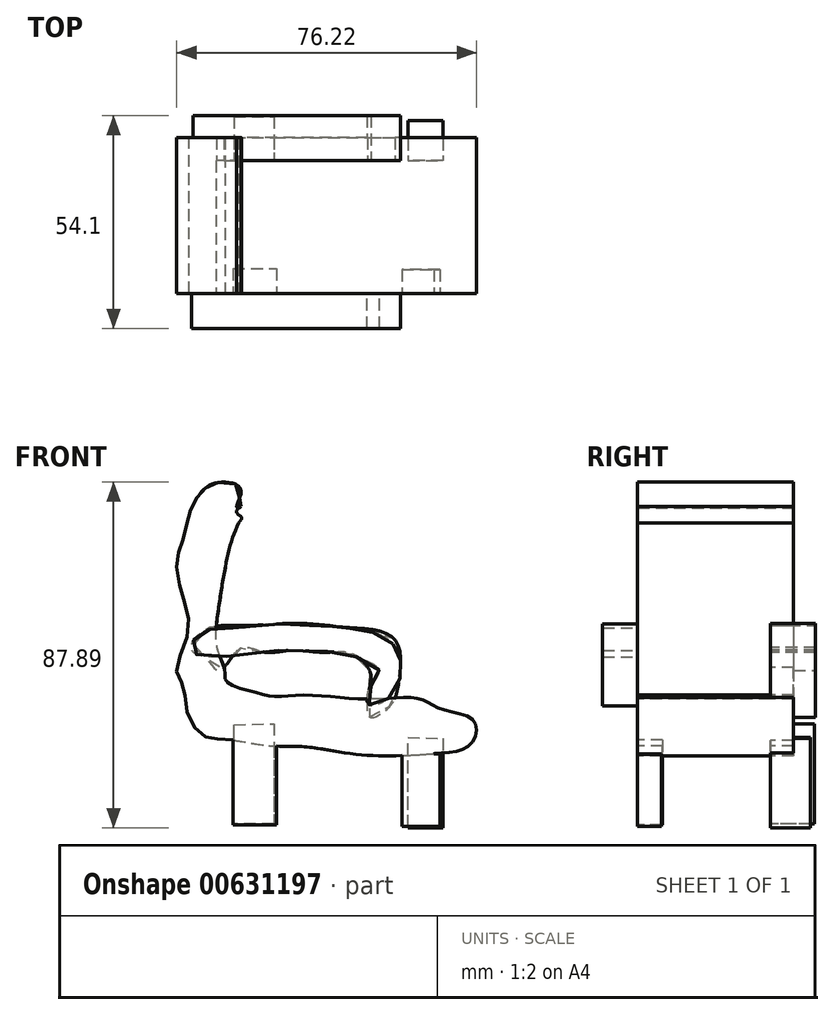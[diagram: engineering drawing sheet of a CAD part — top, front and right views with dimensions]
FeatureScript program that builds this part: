
annotation { "Feature Type Name" : "Feature", "Feature Type Description" : "" }
export const myFeature = defineFeature(function(context is Context, id is Id, definition is map)
    precondition{}
    {
        {
            var Q0;
            Q0=qCreatedBy(makeId("Front.planeOp"),FACE);
            var sketch = newSketch(context, id + "F0", { "sketchPlane" : qUnion([Q0])});
            skFitSpline(sketch, "E0", {"points": [v(-32.6, 41.62) * mm, v(-32.63, 45.08) * mm, v(-38.39, 47.76) * mm, v(-42.92, 45.16) * mm, v(-45.8, 40) * mm, v(-47.39, 33.25) * mm, v(-48.99, 27.76) * mm, v(-47.37, 18.5) * mm, v(-46.09, 9.77) * mm, v(-49, 0) * mm, v(-47.36, -4.04) * mm, v(-46.13, -11.42) * mm, v(-41.64, -16.92) * mm, v(-36.74, -17.5) * mm, v(-25.54, -19.12) * mm, v(-16.21, -19.42) * mm, v(-5.62, -21.05) * mm, v(6.26, -21.69) * mm, v(17.82, -21.06) * mm, v(25.6, -18.86) * mm, v(26.58, -12.94) * mm, v(18.16, -9.8) * mm, v(12.68, -7.2) * mm, v(3.37, -7.23) * mm, v(-7.23, -6.9) * mm, v(-17.8, -6.25) * mm, v(-24.25, -6.6) * mm, v(-30.04, -5.31) * mm, v(-36.45, -2.76) * mm, v(-36.78, 0) * mm, v(-38.68, 5.64) * mm, v(-38.4, 15.58) * mm, v(-36.78, 25.52) * mm, v(-35.04, 32.96) * mm, v(-32.57, 38.94) * mm], "startDerivative": vector(-388.44, -209.27) * mm, "endDerivative": vector(110.78, 242.37) * mm});
            skFitSpline(sketch, "E1", {"points": [v(-32.6, 41.62) * mm, v(-32.57, 38.94) * mm, v(-33.58, 36.74) * mm], "startDerivative": vector(-15.11, -8.14) * mm, "endDerivative": vector(-1.6, -6.6) * mm});
            skSolve(sketch);
        }
        {
            var Q0;
            Q0 = qSketchRegion(id + "F0", true);
            extrude(context, id + "F1", {"entities" : qUnion([Q0]), "oppositeDirection" : true, "depth" : 39.62 * mm, "offsetDistance" : 25.4 * mm});
        }
        {
            var Q0;
            Q0=qCreatedBy(makeId("Front.planeOp"),FACE);
            var sketch = newSketch(context, id + "F2", { "sketchPlane" : qUnion([Q0])});
            skFitSpline(sketch, "E2", {"points": [v(-40.63, 10.44) * mm, v(-32.92, 10.76) * mm, v(-25.54, 11.72) * mm, v(-14.61, 11.4) * mm, v(-8.2, 11.08) * mm, v(-3.37, 10.44) * mm, v(4.34, 8.2) * mm, v(7.55, 3.7) * mm, v(7.87, 0) * mm, v(5.94, -5.94) * mm, v(0, -8.83) * mm, v(0, -4.66) * mm, v(2.4, 0) * mm, v(-6.9, 4.34) * mm, v(-15.9, 4.98) * mm, v(-24.25, 4.98) * mm, v(-31.96, 4.01) * mm, v(-44.49, 4.34) * mm, v(-44.8, 7.55) * mm, v(-40.63, 10.44) * mm]});
            skSolve(sketch);
        }
        {
            var Q0;
            Q0=makeQuery(id+"F2.imprint","IMPRINT",FACE,{"disambiguationData":[TD([[makeQuery(id+"F2.imprint","IMPRINT",EDGE,{"derivedFrom":sQuery(id+"F2.wireOp",EDGE,"E2")}),-1.0]])]});
            extrude(context, id + "F3", {"entities" : qUnion([Q0]), "operationType" : NewBodyOperationType.ADD, "depth" : 8.9 * mm, "offsetDistance" : 25.4 * mm});
        }
        {
            var Q0;
            Q0=qCreatedBy(makeId("Front.planeOp"),FACE);
            var sketch = newSketch(context, id + "F4", { "sketchPlane" : qUnion([Q0])});
            skLineSegment(sketch, "E3", {"start": v(17.83, -21.36) * mm, "end": v(17.83, -39.67) * mm});
            skLineSegment(sketch, "E4", {"start": v(17.83, -39.67) * mm, "end": v(8.2, -39.67) * mm});
            skLineSegment(sketch, "E5", {"start": v(8.2, -39.67) * mm, "end": v(8.2, -23.29) * mm});
            skLineSegment(sketch, "E6", {"start": v(8.2, -23.29) * mm, "end": v(8.2, -20.07) * mm});
            skLineSegment(sketch, "E7", {"start": v(8.2, -20.07) * mm, "end": v(17.83, -21.36) * mm});
            skSolve(sketch);
        }
        {
            var Q0;
            Q0 = qSketchRegion(id + "F4", true);
            extrude(context, id + "F5", {"entities" : qUnion([Q0]), "operationType" : NewBodyOperationType.ADD, "oppositeDirection" : true, "depth" : 6.1 * mm, "offsetDistance" : 25.4 * mm});
        }
        {
            var Q0;
            Q0=qCreatedBy(makeId("Front.planeOp"),FACE);
            var sketch = newSketch(context, id + "F6", { "sketchPlane" : qUnion([Q0])});
            skLineSegment(sketch, "E8", {"start": v(-34.72, -14.2) * mm, "end": v(-34.72, -39.3) * mm});
            skLineSegment(sketch, "E9", {"start": v(-34.72, -39.3) * mm, "end": v(-23.6, -39.3) * mm});
            skLineSegment(sketch, "E10", {"start": v(-23.6, -39.3) * mm, "end": v(-23.6, -14.08) * mm});
            skLineSegment(sketch, "E11", {"start": v(-23.6, -14.08) * mm, "end": v(-34.72, -14.2) * mm});
            skSolve(sketch);
        }
        {
            var Q0;
            Q0 = qSketchRegion(id + "F6", true);
            extrude(context, id + "F7", {"entities" : qUnion([Q0]), "operationType" : NewBodyOperationType.ADD, "oppositeDirection" : true, "depth" : 6.35 * mm, "offsetDistance" : 25.4 * mm});
        }
        {
            var Q0;
            Q0=qCreatedBy(makeId("Front.planeOp"),FACE);
            cPlane(context, id + "F8", {"entities" : qUnion([Q0]), "cplaneType" : CPlaneType.OFFSET, "offset" : 33.78 * mm, "oppositeDirection" : true, "width" : 152.4 * mm, "height" : 152.4 * mm});
        }
        {
            var Q0;
            Q0=qCreatedBy(id+"F8.planeOp",FACE);
            var sketch = newSketch(context, id + "F9", { "sketchPlane" : qUnion([Q0])});
            skFitSpline(sketch, "E12", {"points": [v(0, -11.81) * mm, v(5.13, -9.14) * mm, v(6.91, -5.57) * mm, v(7.8, 0) * mm, v(6.02, 8.25) * mm, v(-5.57, 10.92) * mm, v(-14.49, 11.81) * mm, v(-23.4, 11.81) * mm, v(-30.98, 11.37) * mm, v(-37.67, 11.37) * mm, v(-42.13, 10.03) * mm, v(-44.8, 6.46) * mm, v(-42.13, 3.79) * mm, v(-38.12, 0) * mm, v(-32.77, 5.57) * mm, v(-26.97, 4.68) * mm, v(-19.84, 5.13) * mm, v(-13.6, 4.68) * mm, v(-9.14, 4.68) * mm, v(-4.24, 4.24) * mm, v(0, 0) * mm, v(0, -4.24) * mm, v(0, -11.81) * mm]});
            skSolve(sketch);
        }
        {
            var Q0;
            Q0 = qSketchRegion(id + "F9", true);
            extrude(context, id + "F10", {"entities" : qUnion([Q0]), "operationType" : NewBodyOperationType.ADD, "oppositeDirection" : true, "depth" : 11.43 * mm, "offsetDistance" : 25.4 * mm});
        }
        {
            var Q0;
            Q0=qCreatedBy(id+"F8.planeOp",FACE);
            var sketch = newSketch(context, id + "F11", { "sketchPlane" : qUnion([Q0])});
            skLineSegment(sketch, "E13", {"start": v(18.62, -17.3) * mm, "end": v(18.62, -40.03) * mm});
            skLineSegment(sketch, "E14", {"start": v(18.62, -40.03) * mm, "end": v(9.71, -40.03) * mm});
            skLineSegment(sketch, "E15", {"start": v(9.71, -40.03) * mm, "end": v(9.71, -17.06) * mm});
            skLineSegment(sketch, "E16", {"start": v(9.71, -17.06) * mm, "end": v(18.62, -17.3) * mm});
            skSolve(sketch);
        }
        {
            var Q0;
            Q0 = qSketchRegion(id + "F11", true);
            extrude(context, id + "F12", {"entities" : qUnion([Q0]), "operationType" : NewBodyOperationType.ADD, "oppositeDirection" : true, "depth" : 10.16 * mm, "offsetDistance" : 25.4 * mm});
        }
        {
            var Q0;
            Q0=qCreatedBy(id+"F8.planeOp",FACE);
            var sketch = newSketch(context, id + "F13", { "sketchPlane" : qUnion([Q0])});
            skLineSegment(sketch, "E17", {"start": v(-24.32, -13.57) * mm, "end": v(-24.32, -39) * mm});
            skLineSegment(sketch, "E18", {"start": v(-24.32, -39) * mm, "end": v(-34.48, -39) * mm});
            skLineSegment(sketch, "E19", {"start": v(-34.48, -39) * mm, "end": v(-34.48, -13.88) * mm});
            skLineSegment(sketch, "E20", {"start": v(-34.48, -13.88) * mm, "end": v(-24.32, -13.57) * mm});
            skSolve(sketch);
        }
        {
            var Q0;
            Q0 = qSketchRegion(id + "F13", true);
            extrude(context, id + "F14", {"entities" : qUnion([Q0]), "operationType" : NewBodyOperationType.ADD, "oppositeDirection" : true, "depth" : 11.18 * mm, "offsetDistance" : 25.4 * mm});
        }
    });
